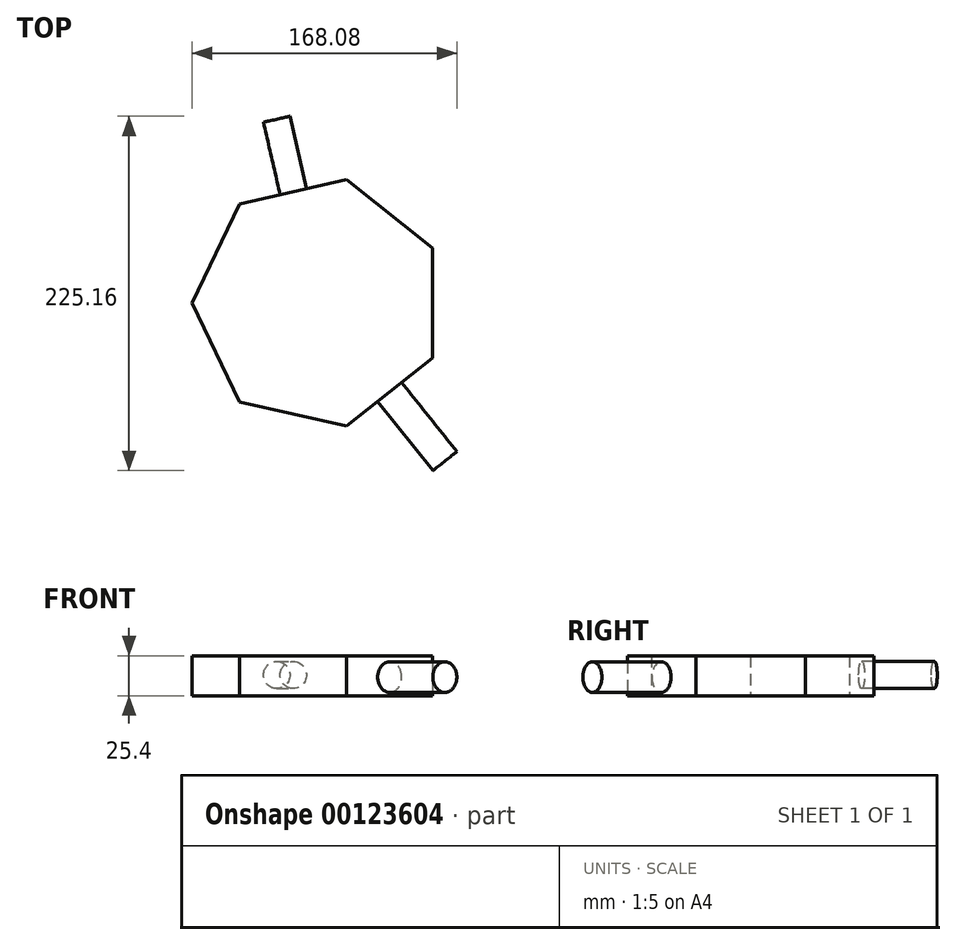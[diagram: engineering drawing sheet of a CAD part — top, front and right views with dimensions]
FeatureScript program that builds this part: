
annotation { "Feature Type Name" : "Feature", "Feature Type Description" : "" }
export const myFeature = defineFeature(function(context is Context, id is Id, definition is map)
    precondition{}
    {
        {
            var Q0;
            Q0=qCreatedBy(makeId("Top.planeOp"),FACE);
            var sketch = newSketch(context, id + "F0", { "sketchPlane" : qUnion([Q0])});
            skCircle(sketch, "E0.cCircle", {"center": v(0, 0) * mm, "radius": 72.36 * mm, "construction": true});
            skLineSegment(sketch, "E0.0", {"start": v(72.36, 34.85) * mm, "end": v(72.36, -34.85) * mm});
            skLineSegment(sketch, "E0.1", {"start": v(72.36, -34.85) * mm, "end": v(17.87, -78.3) * mm});
            skLineSegment(sketch, "E0.2", {"start": v(17.87, -78.3) * mm, "end": v(-50.08, -62.8) * mm});
            skLineSegment(sketch, "E0.3", {"start": v(-50.08, -62.8) * mm, "end": v(-80.32, 0) * mm});
            skLineSegment(sketch, "E0.4", {"start": v(-80.32, 0) * mm, "end": v(-50.08, 62.8) * mm});
            skLineSegment(sketch, "E0.5", {"start": v(-50.08, 62.8) * mm, "end": v(17.87, 78.3) * mm});
            skLineSegment(sketch, "E0.6", {"start": v(17.87, 78.3) * mm, "end": v(72.36, 34.85) * mm});
            skPoint(sketch, "E0.0.midPoint", {"position": v(72.36, 0) * mm});
            skSolve(sketch);
        }
        {
            var Q0;
            Q0=makeQuery(id+"F0.imprint","IMPRINT",FACE,{"disambiguationData":[TD([[makeQuery(id+"F0.imprint","IMPRINT",EDGE,{"derivedFrom":sQuery(id+"F0.wireOp",EDGE,"E0.0")}),-1.0]])]});
            var Q1;
            Q1 = qSketchRegion(id + "F0", true);
            extrude(context, id + "F1", {"entities" : qUnion([Q0, Q1]), "depth" : 25.4 * mm});
        }
        {
            var Q0;
            Q0=makeQuery(id+"F1.opExtrude","SWEPT_FACE",FACE,{"disambiguationData":[OSD([sQuery(id+"F0.wireOp",EDGE,"E0.1")])]});
            var sketch = newSketch(context, id + "F2", { "sketchPlane" : qUnion([Q0])});
            skCircle(sketch, "E1", {"center": v(0, 11.8) * mm, "radius": 9.71 * mm});
            skSolve(sketch);
        }
        {
            var Q0;
            Q0=makeQuery(id+"F2.imprint","IMPRINT",FACE,{"disambiguationData":[TD([[makeQuery(id+"F2.imprint","IMPRINT",EDGE,{"derivedFrom":sQuery(id+"F2.wireOp",EDGE,"E1")}),1.0]])]});
            extrude(context, id + "F3", {"entities" : qUnion([Q0]), "operationType" : NewBodyOperationType.ADD, "depth" : 56.2 * mm});
        }
        {
            var Q0;
            Q0=makeQuery(id+"F1.opExtrude","SWEPT_FACE",FACE,{"disambiguationData":[OSD([sQuery(id+"F0.wireOp",EDGE,"E0.5")])]});
            var sketch = newSketch(context, id + "F4", { "sketchPlane" : qUnion([Q0])});
            skCircle(sketch, "E2", {"center": v(0, 13.15) * mm, "radius": 8.57 * mm});
            skSolve(sketch);
        }
        {
            var Q0;
            Q0=makeQuery(id+"F4.imprint","IMPRINT",FACE,{"disambiguationData":[TD([[makeQuery(id+"F4.imprint","IMPRINT",EDGE,{"derivedFrom":sQuery(id+"F4.wireOp",EDGE,"E2")}),1.0]])]});
            extrude(context, id + "F5", {"entities" : qUnion([Q0]), "operationType" : NewBodyOperationType.ADD, "depth" : 47.31 * mm});
        }
    });
